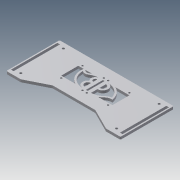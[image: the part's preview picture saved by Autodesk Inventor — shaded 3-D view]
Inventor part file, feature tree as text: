
AUTODESK INVENTOR PART (.ipt)
format: ipt  version: 2014 (Build 180170000, 170)  size: 252,928 bytes
history: native  units: mm
features: extrude x5, sketch x5, fillet x1
ambient origin geometry x8: Origin, YZ Plane, XZ Plane, XY Plane, X Axis, Y Axis, Z Axis, Center Point
bodies: Solid1 (feature_tree)
feature tree (11):
  extrude  "Extrusion1"  Depth=268.0mm
  extrude  "Extrusion2"  Depth=25.0mm
  extrude  "Extrusion5"  Depth=50.0mm
  fillet  "Fillet1"  Radius=3.0mm
  extrude  "Extrusion6"  Depth=21.5mm
  extrude  "Extrusion7"  Depth=12.5mm
  sketch  "Sketch1"  dims[d1=125.0mm d2=268.0mm]
  sketch  "Sketch2"  dims[d4=6.0mm d5=0.0mm d6=25.0mm]
  sketch  "Sketch7"  dims[d7=34.0mm d9=50.0mm d10=3.0mm d11=0.0mm]
  sketch  "Sketch8"  dims[d47=34.0mm d48=21.5mm]
  sketch  "Sketch9"  dims[d49=21.5mm d50=12.5mm d51=12.5mm d56=2.875mm d57=6.25mm d58=2.875mm d60=8.0mm d61=5.4mm d62=108.9mm d63=10.0mm d64=0.0mm d65=2.0mm d66=8.1mm d67=50.0mm d68=60.0mm d69=100.0mm d70=25.0mm d71=4.3mm d72=10.0mm d73=0.0mm d74=4.0mm d75=40.0mm d76=50.0mm d77=25.0mm d78=12.5mm d79=5.0mm d80=8.0mm d81=22.0mm d82=15.0mm d83=34.0mm d84=9.0mm d85=4.0mm d86=4.0mm d87=60.0mm d88=8.0mm d89=5.0mm d90=10.0mm d91=5.0mm d92=34.0mm d93=35.0mm d94=20.0mm d95=6.0mm d96=60.0mm d97=4.0mm d99=4.0mm d100=10.0mm d101=0.0mm]
